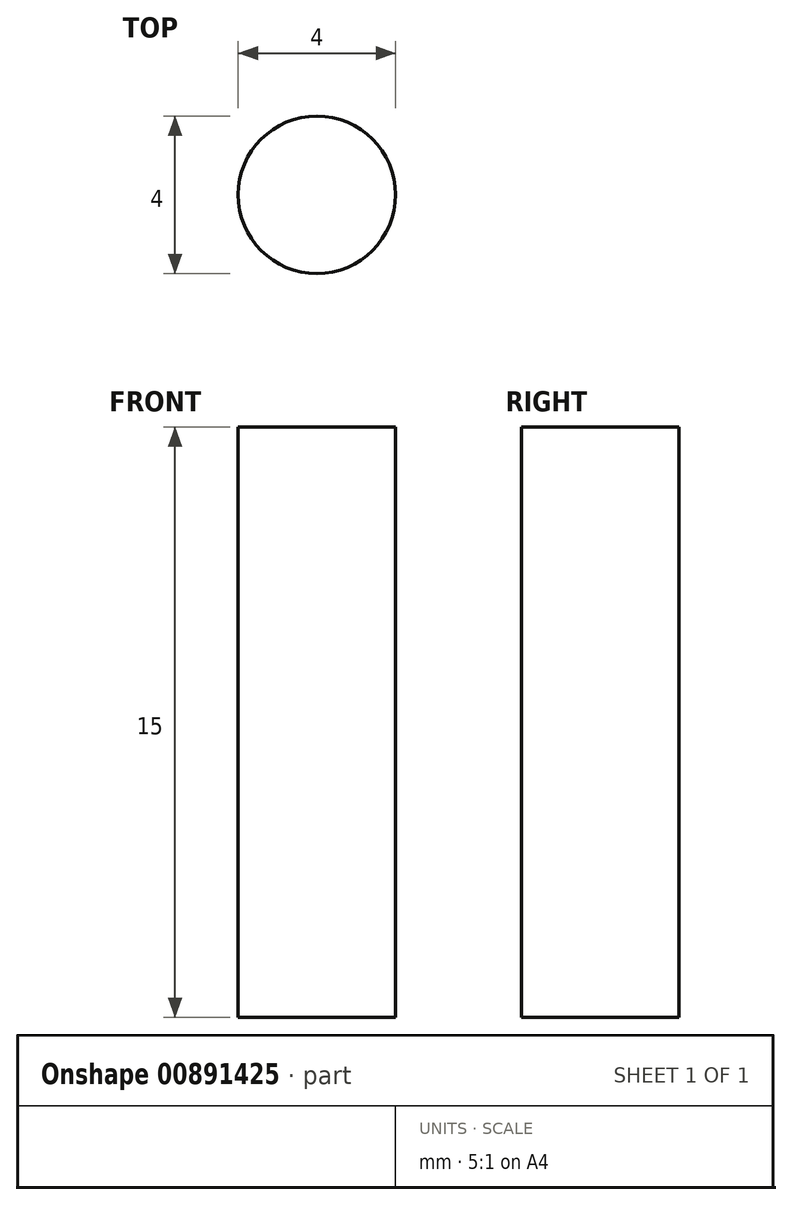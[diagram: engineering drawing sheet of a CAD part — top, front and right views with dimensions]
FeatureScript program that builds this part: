
annotation { "Feature Type Name" : "Feature", "Feature Type Description" : "" }
export const myFeature = defineFeature(function(context is Context, id is Id, definition is map)
    precondition{}
    {
        {
            var Q0;
            Q0=qCreatedBy(makeId("Top.planeOp"),FACE);
            var sketch = newSketch(context, id + "F0", { "sketchPlane" : qUnion([Q0])});
            skCircle(sketch, "E0", {"center": v(0, 0) * mm, "radius": 2 * mm});
            skSolve(sketch);
        }
        {
            var Q0;
            Q0=makeQuery(id+"F0.imprint","IMPRINT",FACE,{"disambiguationData":[TD([[makeQuery(id+"F0.imprint","IMPRINT",EDGE,{"derivedFrom":sQuery(id+"F0.wireOp",EDGE,"E0")}),1.0]])]});
            extrude(context, id + "F1", {"entities" : qUnion([Q0]), "depth" : 15 * mm, "offsetDistance" : 25 * mm});
        }
    });
